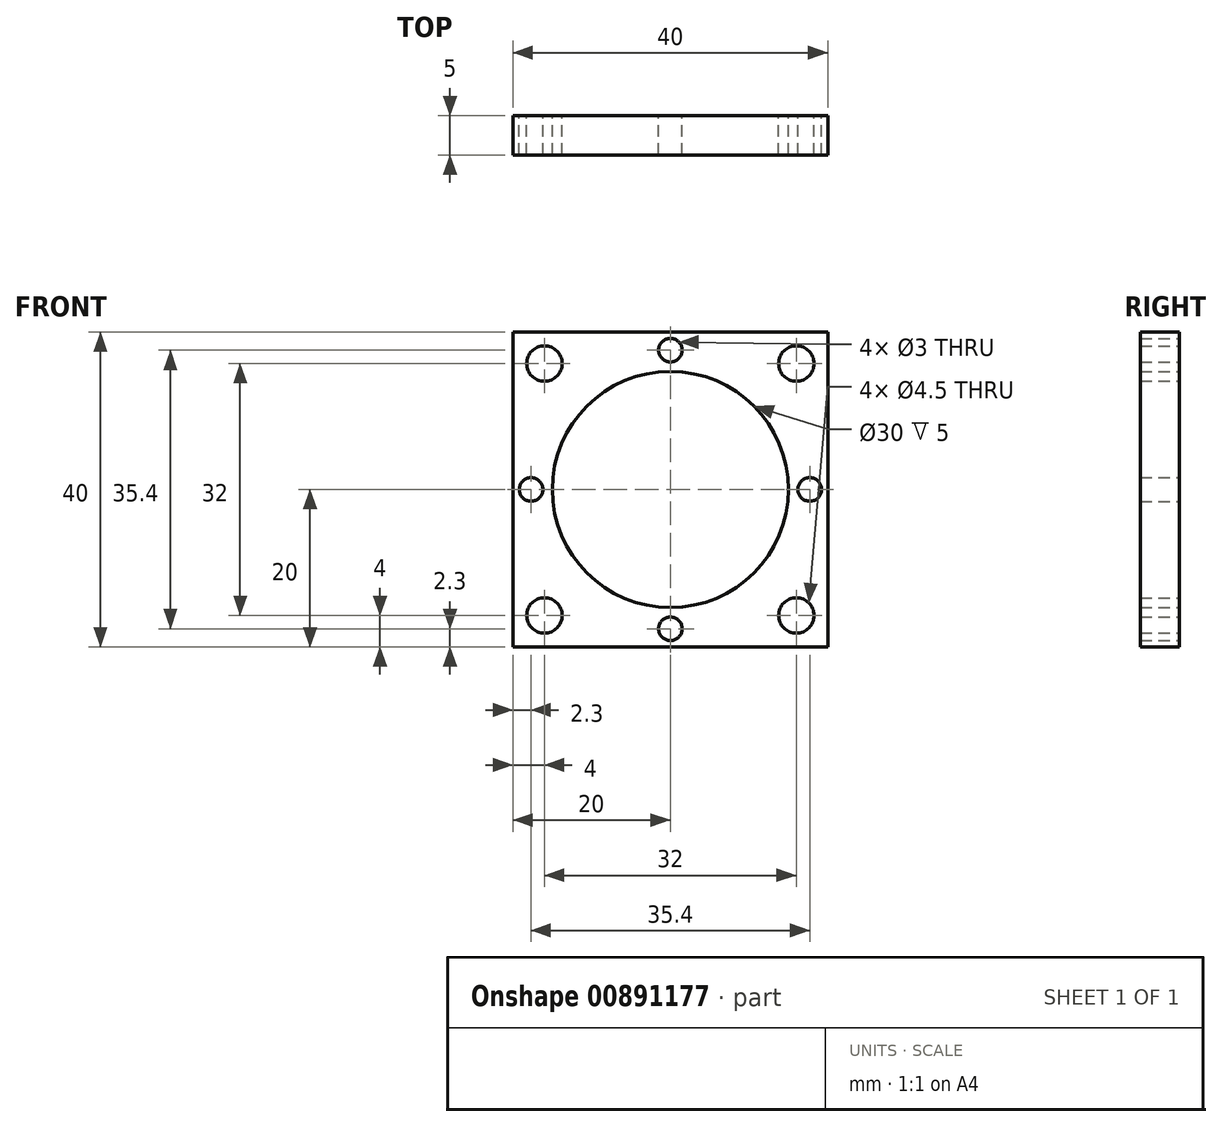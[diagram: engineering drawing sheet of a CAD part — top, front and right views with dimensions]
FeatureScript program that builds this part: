
annotation { "Feature Type Name" : "Feature", "Feature Type Description" : "" }
export const myFeature = defineFeature(function(context is Context, id is Id, definition is map)
    precondition{}
    {
        {
            var Q0;
            Q0=qCreatedBy(makeId("Front.planeOp"),FACE);
            var sketch = newSketch(context, id + "F0", { "sketchPlane" : qUnion([Q0])});
            skLineSegment(sketch, "E0.bottom", {"start": v(-20, -20) * mm, "end": v(20, -20) * mm});
            skLineSegment(sketch, "E0.top", {"start": v(-20, 20) * mm, "end": v(20, 20) * mm});
            skLineSegment(sketch, "E0.left", {"start": v(-20, -20) * mm, "end": v(-20, 20) * mm});
            skLineSegment(sketch, "E0.right", {"start": v(20, -20) * mm, "end": v(20, 20) * mm});
            skPoint(sketch, "E0.middle", {"position": v(0, 0) * mm});
            skLineSegment(sketch, "E1.bottom", {"start": v(-16, -16) * mm, "end": v(16, -16) * mm, "construction": true});
            skLineSegment(sketch, "E1.top", {"start": v(-16, 16) * mm, "end": v(16, 16) * mm, "construction": true});
            skLineSegment(sketch, "E1.left", {"start": v(-16, -16) * mm, "end": v(-16, 16) * mm, "construction": true});
            skLineSegment(sketch, "E1.right", {"start": v(16, -16) * mm, "end": v(16, 16) * mm, "construction": true});
            skCircle(sketch, "E2", {"center": v(-16, 16) * mm, "radius": 2.25 * mm});
            skLineSegment(sketch, "E3", {"start": v(0, 20) * mm, "end": v(0, -20) * mm, "construction": true});
            skLineSegment(sketch, "E4", {"start": v(20, 0) * mm, "end": v(-20, 0) * mm, "construction": true});
            skCircle(sketch, "E5", {"center": v(0, 17.7) * mm, "radius": 1.5 * mm});
            skCircle(sketch, "E6.MirrorC", {"center": v(0, -17.7) * mm, "radius": 1.5 * mm});
            skCircle(sketch, "E7.MirrorC", {"center": v(16, 16) * mm, "radius": 2.25 * mm});
            skCircle(sketch, "E8.MirrorC", {"center": v(16, -16) * mm, "radius": 2.25 * mm});
            skCircle(sketch, "E9.MirrorC", {"center": v(-16, -16) * mm, "radius": 2.25 * mm});
            skCircle(sketch, "E10", {"center": v(0, 0) * mm, "radius": 15 * mm});
            skLineSegment(sketch, "E11", {"start": v(0, 0) * mm, "end": v(0, 17.7) * mm, "construction": true});
            skLineSegment(sketch, "E12", {"start": v(0, 17.7) * mm, "end": v(9.75, 17.74) * mm, "construction": true});
            skCircle(sketch, "E13", {"center": v(0, 0) * mm, "radius": 17.7 * mm, "construction": true});
            skCircle(sketch, "E14", {"center": v(-17.7, 0) * mm, "radius": 1.5 * mm});
            skCircle(sketch, "E15.MirrorC", {"center": v(17.7, 0) * mm, "radius": 1.5 * mm});
            skSolve(sketch);
        }
        {
            var Q0;
            Q0 = qSketchRegion(id + "F0", true);
            extrude(context, id + "F1", {"entities" : qUnion([Q0]), "depth" : 5 * mm, "offsetDistance" : 25 * mm});
        }
    });
